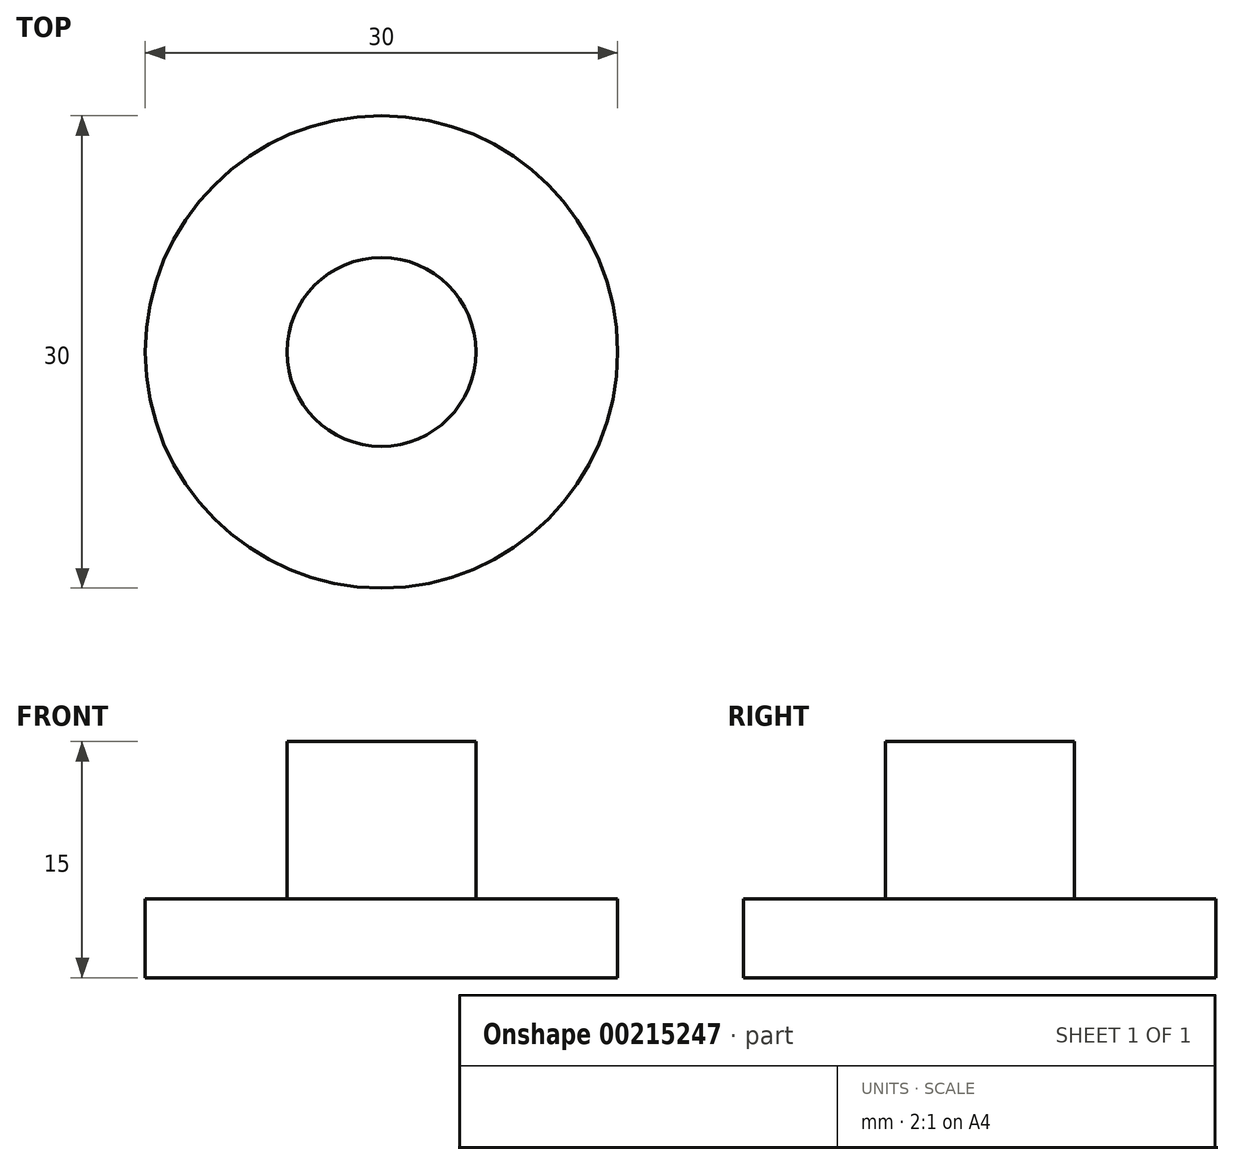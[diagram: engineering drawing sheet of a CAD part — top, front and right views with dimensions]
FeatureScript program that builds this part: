
annotation { "Feature Type Name" : "Feature", "Feature Type Description" : "" }
export const myFeature = defineFeature(function(context is Context, id is Id, definition is map)
    precondition{}
    {
        {
            var Q0;
            Q0=qCreatedBy(makeId("Top.planeOp"),FACE);
            var sketch = newSketch(context, id + "F0", { "sketchPlane" : qUnion([Q0])});
            skCircle(sketch, "E0", {"center": v(0, 0) * mm, "radius": 15 * mm});
            skSolve(sketch);
        }
        {
            var Q0;
            Q0=makeQuery(id+"F0.imprint","IMPRINT",FACE,{"disambiguationData":[TD([[makeQuery(id+"F0.imprint","IMPRINT",EDGE,{"derivedFrom":sQuery(id+"F0.wireOp",EDGE,"E0")}),1.0]])]});
            extrude(context, id + "F1", {"entities" : qUnion([Q0]), "depth" : 5 * mm});
        }
        {
            var Q0;
            Q0=makeQuery(id+"F1.opExtrude","CAP_FACE",FACE,{"disambiguationData":[OSD([sQuery(id+"F0.wireOp",EDGE,"E0")])],"isStart":false});
            var sketch = newSketch(context, id + "F2", { "sketchPlane" : qUnion([Q0])});
            skArc(sketch, "E1", {"start": v(0, 12) * mm, "mid": v(5.34, 10.75) * mm, "end": v(9.57, 7.24) * mm});
            skArc(sketch, "E2.0.startCap", {"start": v(0, 10.2) * mm, "mid": v(-1.8, 12) * mm, "end": v(0, 13.8) * mm});
            skArc(sketch, "E2.0.endCap", {"start": v(11, 8.33) * mm, "mid": v(10.65, 5.8) * mm, "end": v(8.13, 6.16) * mm});
            skArc(sketch, "E2.0.left", {"start": v(0, 13.8) * mm, "mid": v(6.14, 12.36) * mm, "end": v(11, 8.33) * mm});
            skArc(sketch, "E2.0.right", {"start": v(0, 10.2) * mm, "mid": v(4.54, 9.13) * mm, "end": v(8.13, 6.16) * mm});
            skArc(sketch, "E3", {"start": v(0, -12) * mm, "mid": v(-6.17, -10.3) * mm, "end": v(-10.58, -5.66) * mm});
            skArc(sketch, "E4.0.startCap", {"start": v(0, -10.2) * mm, "mid": v(1.8, -12) * mm, "end": v(0, -13.8) * mm});
            skArc(sketch, "E4.0.endCap", {"start": v(-12.17, -6.5) * mm, "mid": v(-11.43, -4.07) * mm, "end": v(-9, -4.81) * mm});
            skArc(sketch, "E4.0.left", {"start": v(0, -13.8) * mm, "mid": v(-7.1, -11.84) * mm, "end": v(-12.17, -6.5) * mm});
            skArc(sketch, "E4.0.right", {"start": v(0, -10.2) * mm, "mid": v(-5.24, -8.75) * mm, "end": v(-9, -4.81) * mm});
            skSolve(sketch);
        }
        {
            var Q0;
            Q0=makeQuery(id+"F2.imprint","IMPRINT",FACE,{"disambiguationData":[TD([[makeQuery(id+"F2.imprint","IMPRINT",EDGE,{"derivedFrom":sQuery(id+"F2.wireOp",EDGE,"E2.0.startCap")}),1.0]])]});
            var sketch = newSketch(context, id + "F3", { "sketchPlane" : qUnion([Q0])});
            skCircle(sketch, "E5", {"center": v(0, 0) * mm, "radius": 6 * mm});
            skSolve(sketch);
        }
        {
            var Q0;
            Q0 = qSketchRegion(id + "F3", true);
            extrude(context, id + "F4", {"entities" : qUnion([Q0]), "operationType" : NewBodyOperationType.ADD, "depth" : 10 * mm});
        }
    });
